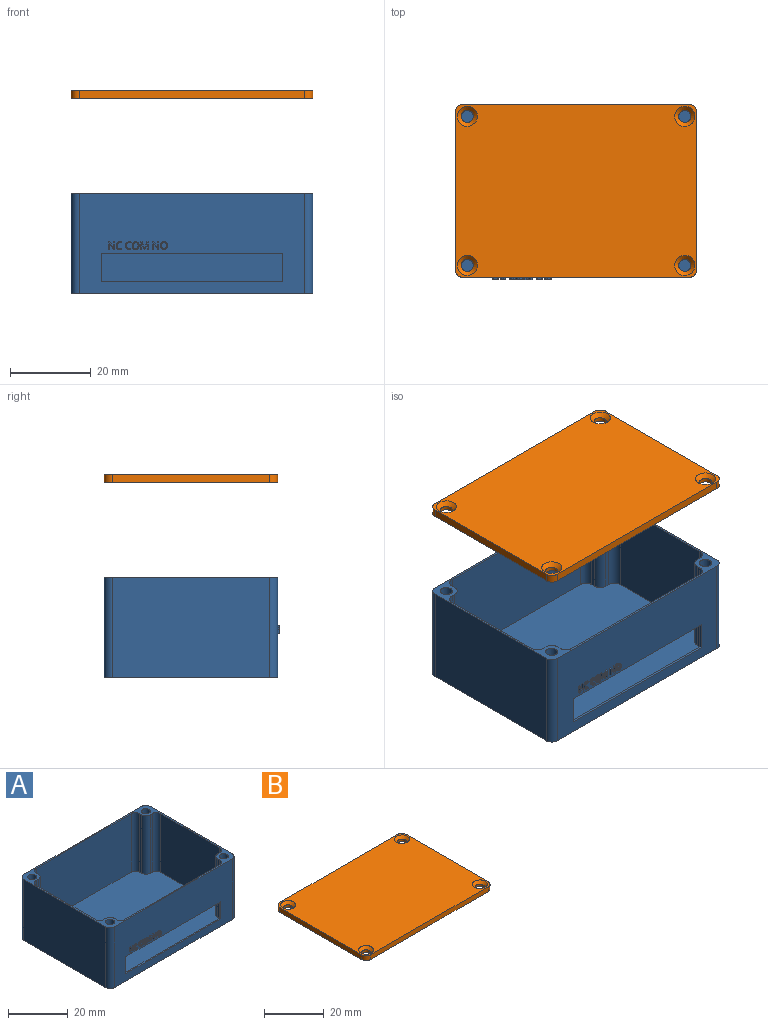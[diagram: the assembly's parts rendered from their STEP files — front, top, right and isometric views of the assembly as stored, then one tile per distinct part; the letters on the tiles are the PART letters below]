
ASSEMBLY  parts=2 mates=1
PART A: 167 faces, bbox 60x43.5x25 mm
  f0: plane 56x25mm, normal (0,-1,0), area 1074.3mm2, adj f7,f11,f29,f30,f44,f45,f46,f47
  f1: plane 45x2mm, normal (0,1,0), area 90mm2, adj f2,f32,f39,f46
  f2: plane 59x42mm, normal (0,0,1), area 2374.6mm2, adj f1,f4,f5,f6,f12,f13,f14,f15
  f3: plane 45x15mm, normal (0,1,0), area 675mm2, adj f7,f32,f39,f47
  f4: plane 28x24mm, normal (-1,0,0), area 672mm2, adj f2,f7,f34,f37
  f5: plane 45x24mm, normal (0,-1,0), area 1080mm2, adj f2,f7,f36,f41
  f6: plane 28x24mm, normal (1,0,0), area 672mm2, adj f2,f7,f38,f43
  f7: plane 60x43mm, normal (0,0,1), area 173.7mm2, adj f0,f3,f4,f5,f6,f8,f9,f10
  f8: plane 56x25mm, normal (0,1,0), area 1400mm2, adj f7,f11,f28,f31
  f9: plane 39x25mm, normal (-1,0,0), area 975mm2, adj f7,f11,f28,f29
  f10: plane 39x25mm, normal (1,0,0), area 975mm2, adj f7,f11,f30,f31
  f11: plane 60x43mm, normal (0,0,-1), area 2576.6mm2, adj f0,f8,f9,f10,f28,f29,f30,f31
  f12: plane 24x1mm, normal (0,-1,0), area 24mm2, adj f2,f7,f42,f43
  f13: plane 24x1mm, normal (1,0,0), area 24mm2, adj f2,f7,f41,f42
  f14: plane 24x1mm, normal (0,1,0), area 24mm2, adj f2,f7,f38,f40
  f15: plane 24x1mm, normal (1,0,0), area 24mm2, adj f2,f7,f39,f40
  f16: plane 24x1mm, normal (0,-1,0), area 24mm2, adj f2,f7,f35,f37
  f17: plane 24x1mm, normal (-1,0,0), area 24mm2, adj f2,f7,f35,f36
  f18: plane 24x1mm, normal (0,1,0), area 24mm2, adj f2,f7,f33,f34
  f19: plane 24x1mm, normal (-1,0,0), area 24mm2, adj f2,f7,f32,f33
  f20: cylinder r=1.5mm len=10mm, axis (0,0,1), area 94.2mm2, adj f7,f21
  f21: plane 3x3mm, normal (0,0,1), area 7.1mm2, adj f20
  f22: cylinder r=1.5mm len=10mm, axis (0,0,1), area 94.2mm2, adj f7,f23
  f23: plane 3x3mm, normal (0,0,1), area 7.1mm2, adj f22
  f24: cylinder r=1.5mm len=10mm, axis (0,0,1), area 94.2mm2, adj f7,f25
  f25: plane 3x3mm, normal (0,0,1), area 7.1mm2, adj f24
  f26: cylinder r=1.5mm len=10mm, axis (0,0,1), area 94.2mm2, adj f7,f27
  f27: plane 3x3mm, normal (0,0,1), area 7.1mm2, adj f26
  f28: cylinder r=2mm len=25mm, axis (0,0,1), area 78.5mm2, adj f7,f8,f9,f11
  f29: cylinder r=2mm len=25mm, axis (0,0,-1), area 78.5mm2, adj f0,f7,f9,f11
  f30: cylinder r=2mm len=25mm, axis (0,0,1), area 78.5mm2, adj f0,f7,f10,f11
  f31: cylinder r=2mm len=25mm, axis (0,0,-1), area 78.5mm2, adj f7,f8,f10,f11
  f32: cylinder r=2mm len=24mm, axis (0,0,1), area 75.4mm2, adj f1,f2,f3,f7,f19,f44
  f33: cylinder r=2mm len=24mm, axis (0,0,1), area 75.4mm2, adj f2,f7,f18,f19
  f34: cylinder r=2mm len=24mm, axis (0,0,1), area 75.4mm2, adj f2,f4,f7,f18
  f35: cylinder r=2mm len=24mm, axis (0,0,1), area 75.4mm2, adj f2,f7,f16,f17
  f36: cylinder r=2mm len=24mm, axis (0,0,1), area 75.4mm2, adj f2,f5,f7,f17
  f37: cylinder r=2mm len=24mm, axis (0,0,-1), area 75.4mm2, adj f2,f4,f7,f16
  f38: cylinder r=2mm len=24mm, axis (0,0,1), area 75.4mm2, adj f2,f6,f7,f14
  f39: cylinder r=2mm len=24mm, axis (0,0,-1), area 75.4mm2, adj f1,f2,f3,f7,f15,f45
  f40: cylinder r=2mm len=24mm, axis (0,0,1), area 75.4mm2, adj f2,f7,f14,f15
  f41: cylinder r=2mm len=24mm, axis (0,0,-1), area 75.4mm2, adj f2,f5,f7,f13
  f42: cylinder r=2mm len=24mm, axis (0,0,1), area 75.4mm2, adj f2,f7,f12,f13
  f43: cylinder r=2mm len=24mm, axis (0,0,-1), area 75.4mm2, adj f2,f6,f7,f12
  f44: plane 7x0.5mm, normal (-1,0,0), area 3.5mm2, adj f0,f32,f46,f47
  f45: plane 7x0.5mm, normal (1,0,0), area 3.5mm2, adj f0,f39,f46,f47
  f46: plane 45x0.5mm, normal (0,0,1), area 22.5mm2, adj f0,f1,f44,f45
  f47: plane 45x0.5mm, normal (0,0,-1), area 22.5mm2, adj f0,f3,f44,f45
  f48: plane 0.5x0.25mm, normal (0,0,-1), area 0.1mm2, adj f0,f49,f62,f63
  f49: plane 1.86x0.5mm, normal (1,0,0), area 0.9mm2, adj f0,f48,f50,f63
  f50: plane 0.5x0.2mm, normal (0,0,1), area 0.1mm2, adj f0,f49,f51,f63
  f51: plane 1.07x0.5mm, normal (-1,0,0), area 0.5mm2, adj f0,f50,f52,f63
  f52: extruded ~0.5x0.27mm, area 0.1mm2, adj f0,f51,f53,f63
  f53: extruded ~0.5x0.22mm, area 0.1mm2, adj f0,f52,f54,f63
  f54: plane 0.5x0.01mm, normal (0,0,1), area 0mm2, adj f0,f53,f55,f63
  f55: plane 1.56x1.01mm, normal (0.84,0,0.55), area 0.9mm2, adj f0,f54,f56,f63
  f56: plane 0.5x0.24mm, normal (0,0,1), area 0.1mm2, adj f0,f55,f57,f63
  f57: plane 1.86x0.5mm, normal (-1,0,0), area 0.9mm2, adj f0,f56,f58,f63
  f58: plane 0.5x0.2mm, normal (0,0,-1), area 0.1mm2, adj f0,f57,f59,f63
  f59: plane 1.06x0.5mm, normal (1,0,0), area 0.5mm2, adj f0,f58,f60,f63
  f60: extruded ~0.5x0.5mm, area 0.3mm2, adj f0,f59,f61,f63
  f61: plane 0.5x0.01mm, normal (0,0,-1), area 0mm2, adj f0,f60,f62,f63
  f62: plane 1.56x1.02mm, normal (-0.84,0,-0.55), area 0.9mm2, adj f0,f48,f61,f63
  f63: plane 1.86x1.45mm, normal (0,-1,0), area 1.1mm2, adj f48,f49,f50,f51,f52,f53,f54,f55
  f64: extruded ~0.5x0.48mm, area 0.3mm2, adj f0,f65,f78,f79
  f65: extruded ~0.5x0.42mm, area 0.2mm2, adj f0,f64,f66,f79
  f66: plane 0.5x0.19mm, normal (0.9,0,-0.44), area 0.1mm2, adj f0,f65,f67,f79
  f67: extruded ~0.51x0.5mm, area 0.3mm2, adj f0,f66,f68,f79
  f68: extruded ~0.5x0.48mm, area 0.2mm2, adj f0,f67,f69,f79
  f69: extruded ~0.5x0.33mm, area 0.2mm2, adj f0,f68,f70,f79
  f70: extruded ~0.5x0.5mm, area 0.3mm2, adj f0,f69,f71,f79
  f71: extruded ~0.71x0.5mm, area 0.4mm2, adj f0,f70,f72,f79
  f72: extruded ~0.63x0.5mm, area 0.4mm2, adj f0,f71,f73,f79
  f73: extruded ~0.5x0.48mm, area 0.2mm2, adj f0,f72,f74,f79
  f74: plane 0.5x0.19mm, normal (1,0,0), area 0.1mm2, adj f0,f73,f75,f79
  f75: extruded ~0.5x0.44mm, area 0.2mm2, adj f0,f74,f76,f79
  f76: extruded ~0.5x0.49mm, area 0.3mm2, adj f0,f75,f77,f79
  f77: extruded ~0.56x0.5mm, area 0.3mm2, adj f0,f76,f78,f79
  f78: extruded ~0.56x0.5mm, area 0.3mm2, adj f0,f64,f77,f79
  f79: plane 1.91x1.41mm, normal (0,-1,0), area 0.8mm2, adj f64,f65,f66,f67,f68,f69,f70,f71
  f80: extruded ~0.5x0.48mm, area 0.3mm2, adj f0,f81,f94,f95
  f81: extruded ~0.5x0.42mm, area 0.2mm2, adj f0,f80,f82,f95
  f82: plane 0.5x0.19mm, normal (0.9,0,-0.44), area 0.1mm2, adj f0,f81,f83,f95
  f83: extruded ~0.51x0.5mm, area 0.3mm2, adj f0,f82,f84,f95
  f84: extruded ~0.5x0.48mm, area 0.2mm2, adj f0,f83,f85,f95
  f85: extruded ~0.5x0.33mm, area 0.2mm2, adj f0,f84,f86,f95
  f86: extruded ~0.5x0.5mm, area 0.3mm2, adj f0,f85,f87,f95
  f87: extruded ~0.71x0.5mm, area 0.4mm2, adj f0,f86,f88,f95
  f88: extruded ~0.63x0.5mm, area 0.4mm2, adj f0,f87,f89,f95
  f89: extruded ~0.5x0.48mm, area 0.2mm2, adj f0,f88,f90,f95
  f90: plane 0.5x0.19mm, normal (1,0,0), area 0.1mm2, adj f0,f89,f91,f95
  f91: extruded ~0.5x0.44mm, area 0.2mm2, adj f0,f90,f92,f95
  f92: extruded ~0.5x0.49mm, area 0.3mm2, adj f0,f91,f93,f95
  f93: extruded ~0.56x0.5mm, area 0.3mm2, adj f0,f92,f94,f95
  f94: extruded ~0.56x0.5mm, area 0.3mm2, adj f0,f80,f93,f95
  f95: plane 1.91x1.41mm, normal (0,-1,0), area 0.8mm2, adj f80,f81,f82,f83,f84,f85,f86,f87
  f96: extruded ~0.57x0.5mm, area 0.3mm2, adj f97,f111,f112,f113
  f97: extruded ~0.57x0.5mm, area 0.3mm2, adj f96,f98,f112,f113
  f98: extruded ~0.5x0.47mm, area 0.3mm2, adj f97,f99,f112,f113
  f99: extruded ~0.5x0.47mm, area 0.3mm2, adj f98,f100,f112,f113
  f100: extruded ~0.57x0.5mm, area 0.3mm2, adj f99,f101,f112,f113
  f101: extruded ~0.57x0.5mm, area 0.3mm2, adj f100,f102,f112,f113
  f102: extruded ~0.5x0.47mm, area 0.3mm2, adj f101,f111,f112,f113
  f103: extruded ~0.7x0.5mm, area 0.4mm2, adj f0,f104,f110,f112
  f104: extruded ~0.7x0.5mm, area 0.4mm2, adj f0,f103,f105,f112
  f105: extruded ~0.63x0.5mm, area 0.3mm2, adj f0,f104,f106,f112
  f106: extruded ~0.64x0.5mm, area 0.4mm2, adj f0,f105,f107,f112
  f107: extruded ~0.7x0.5mm, area 0.4mm2, adj f0,f106,f108,f112
  f108: extruded ~0.71x0.5mm, area 0.4mm2, adj f0,f107,f109,f112
  f109: extruded ~0.63x0.5mm, area 0.4mm2, adj f0,f108,f110,f112
  f110: extruded ~0.63x0.5mm, area 0.4mm2, adj f0,f103,f109,f112
  f111: extruded ~0.5x0.47mm, area 0.3mm2, adj f96,f102,f112,f113
  f112: plane 1.92x1.71mm, normal (0,-1,0), area 1.1mm2, adj f96,f97,f98,f99,f100,f101,f102,f103
  f113: plane 1.53x1.25mm, normal (0,-1,0), area 1.6mm2, adj f96,f97,f98,f99,f100,f101,f102,f111
  f114: plane 1.65x0.63mm, normal (-0.93,0,-0.36), area 0.9mm2, adj f0,f115,f131,f132
  f115: plane 0.5x0.17mm, normal (0,0,-1), area 0.1mm2, adj f0,f114,f116,f132
  f116: plane 1.65x0.64mm, normal (0.93,0,-0.36), area 0.9mm2, adj f0,f115,f117,f132
  f117: plane 0.5x0.01mm, normal (0,0,-1), area 0mm2, adj f0,f116,f118,f132
  f118: extruded ~0.5x0.45mm, area 0.2mm2, adj f0,f117,f119,f132
  f119: plane 1.2x0.5mm, normal (-1,0,0), area 0.6mm2, adj f0,f118,f120,f132
  f120: plane 0.5x0.22mm, normal (0,0,-1), area 0.1mm2, adj f0,f119,f121,f132
  f121: plane 1.86x0.5mm, normal (1,0,0), area 0.9mm2, adj f0,f120,f122,f132
  f122: plane 0.5x0.32mm, normal (0,0,1), area 0.2mm2, adj f0,f121,f123,f132
  f123: plane 1.54x0.59mm, normal (-0.93,0,0.36), area 0.8mm2, adj f0,f122,f124,f132
  f124: plane 0.5x0.01mm, normal (0,0,1), area 0mm2, adj f0,f123,f125,f132
  f125: plane 1.54x0.59mm, normal (0.93,0,0.36), area 0.8mm2, adj f0,f124,f126,f132
  f126: plane 0.5x0.33mm, normal (0,0,1), area 0.2mm2, adj f0,f125,f127,f132
  f127: plane 1.86x0.5mm, normal (-1,0,0), area 0.9mm2, adj f0,f126,f128,f132
  f128: plane 0.5x0.2mm, normal (0,0,-1), area 0.1mm2, adj f0,f127,f129,f132
  f129: plane 1.18x0.5mm, normal (1,0,0), area 0.6mm2, adj f0,f128,f130,f132
  f130: extruded ~0.5x0.47mm, area 0.2mm2, adj f0,f129,f131,f132
  f131: plane 0.5x0.01mm, normal (0,0,-1), area 0mm2, adj f0,f114,f130,f132
  f132: plane 1.86x1.84mm, normal (0,-1,0), area 1.5mm2, adj f114,f115,f116,f117,f118,f119,f120,f121
  f133: plane 0.5x0.25mm, normal (0,0,-1), area 0.1mm2, adj f0,f134,f147,f148
  f134: plane 1.86x0.5mm, normal (1,0,0), area 0.9mm2, adj f0,f133,f135,f148
  f135: plane 0.5x0.2mm, normal (0,0,1), area 0.1mm2, adj f0,f134,f136,f148
  f136: plane 1.07x0.5mm, normal (-1,0,0), area 0.5mm2, adj f0,f135,f137,f148
  f137: extruded ~0.5x0.27mm, area 0.1mm2, adj f0,f136,f138,f148
  f138: extruded ~0.5x0.22mm, area 0.1mm2, adj f0,f137,f139,f148
  f139: plane 0.5x0.01mm, normal (0,0,1), area 0mm2, adj f0,f138,f140,f148
  f140: plane 1.56x1.01mm, normal (0.84,0,0.55), area 0.9mm2, adj f0,f139,f141,f148
  f141: plane 0.5x0.24mm, normal (0,0,1), area 0.1mm2, adj f0,f140,f142,f148
  f142: plane 1.86x0.5mm, normal (-1,0,0), area 0.9mm2, adj f0,f141,f143,f148
  f143: plane 0.5x0.2mm, normal (0,0,-1), area 0.1mm2, adj f0,f142,f144,f148
  f144: plane 1.06x0.5mm, normal (1,0,0), area 0.5mm2, adj f0,f143,f145,f148
  f145: extruded ~0.5x0.5mm, area 0.3mm2, adj f0,f144,f146,f148
  f146: plane 0.5x0.01mm, normal (0,0,-1), area 0mm2, adj f0,f145,f147,f148
  f147: plane 1.56x1.02mm, normal (-0.84,0,-0.55), area 0.9mm2, adj f0,f133,f146,f148
  f148: plane 1.86x1.45mm, normal (0,-1,0), area 1.1mm2, adj f133,f134,f135,f136,f137,f138,f139,f140
  f149: extruded ~0.57x0.5mm, area 0.3mm2, adj f150,f164,f165,f166
  f150: extruded ~0.57x0.5mm, area 0.3mm2, adj f149,f151,f165,f166
  f151: extruded ~0.5x0.47mm, area 0.3mm2, adj f150,f152,f165,f166
  f152: extruded ~0.5x0.47mm, area 0.3mm2, adj f151,f153,f165,f166
  f153: extruded ~0.57x0.5mm, area 0.3mm2, adj f152,f154,f165,f166
  f154: extruded ~0.57x0.5mm, area 0.3mm2, adj f153,f155,f165,f166
  f155: extruded ~0.5x0.47mm, area 0.3mm2, adj f154,f164,f165,f166
  f156: extruded ~0.7x0.5mm, area 0.4mm2, adj f0,f157,f163,f165
  f157: extruded ~0.7x0.5mm, area 0.4mm2, adj f0,f156,f158,f165
  f158: extruded ~0.63x0.5mm, area 0.3mm2, adj f0,f157,f159,f165
  f159: extruded ~0.64x0.5mm, area 0.4mm2, adj f0,f158,f160,f165
  f160: extruded ~0.7x0.5mm, area 0.4mm2, adj f0,f159,f161,f165
  f161: extruded ~0.71x0.5mm, area 0.4mm2, adj f0,f160,f162,f165
  f162: extruded ~0.63x0.5mm, area 0.4mm2, adj f0,f161,f163,f165
  f163: extruded ~0.63x0.5mm, area 0.4mm2, adj f0,f156,f162,f165
  f164: extruded ~0.5x0.47mm, area 0.3mm2, adj f149,f155,f165,f166
  f165: plane 1.92x1.71mm, normal (0,-1,0), area 1.1mm2, adj f149,f150,f151,f152,f153,f154,f155,f156
  f166: plane 1.53x1.25mm, normal (0,-1,0), area 1.6mm2, adj f149,f150,f151,f152,f153,f154,f155,f164
PART B: 18 faces, bbox 60x43x2 mm
  f0: plane 56x2mm, normal (0,1,0), area 112mm2, adj f4,f5,f14,f17
  f1: plane 39x2mm, normal (-1,0,0), area 78mm2, adj f4,f5,f14,f15
  f2: plane 56x2mm, normal (0,-1,0), area 112mm2, adj f4,f5,f15,f16
  f3: plane 39x2mm, normal (1,0,0), area 78mm2, adj f4,f5,f16,f17
  f4: plane 60x43mm, normal (0,0,1), area 2498mm2, adj f0,f1,f2,f3,f10,f11,f12,f13
  f5: plane 60x43mm, normal (0,0,-1), area 2548.3mm2, adj f0,f1,f2,f3,f6,f7,f8,f9
  f6: cylinder r=1.5mm len=3mm, axis (0,0,1), area 9.4mm2, adj f5,f10
  f7: cylinder r=1.5mm len=3mm, axis (0,0,1), area 9.4mm2, adj f5,f11
  f8: cylinder r=1.5mm len=3mm, axis (0,0,1), area 9.4mm2, adj f5,f12
  f9: cylinder r=1.5mm len=3mm, axis (0,0,1), area 9.4mm2, adj f5,f13
  f10: cone r=1.5mm half-angle=45deg, axis (0,0,1), area 17.8mm2, adj f4,f6
  f11: cone r=1.5mm half-angle=45deg, axis (0,0,1), area 17.8mm2, adj f4,f7
  f12: cone r=1.5mm half-angle=45deg, axis (0,0,1), area 17.8mm2, adj f4,f8
  f13: cone r=1.5mm half-angle=45deg, axis (0,0,1), area 17.8mm2, adj f4,f9
  f14: cylinder r=2mm len=2mm, axis (0,0,1), area 6.3mm2, adj f0,f1,f4,f5
  f15: cylinder r=2mm len=2mm, axis (0,0,-1), area 6.3mm2, adj f1,f2,f4,f5
  f16: cylinder r=2mm len=2mm, axis (0,0,1), area 6.3mm2, adj f2,f3,f4,f5
  f17: cylinder r=2mm len=2mm, axis (0,0,-1), area 6.3mm2, adj f0,f3,f4,f5
PLACE A t=(30.02,33.08,12.46)mm fixed
PLACE B t=(107.11,104.17,61.08)mm
MATE slider A.f24 <-> B.f8  axis (0,0,1) through (96.38,57.11,37.46)mm
